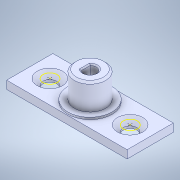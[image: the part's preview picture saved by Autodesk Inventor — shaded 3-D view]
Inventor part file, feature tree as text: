
AUTODESK INVENTOR PART (.ipt)
format: ipt  version: 2021 (Build 250183000, 183)  size: 167,424 bytes
history: native  units: in
note: dims shown in document units (in); Inventor stores cm internally (conversion verified against a paired STEP export)
features: sketch x5, extrude x3, other x3, chamfer x2, reference x2, hole x1, projected_geometry x1
ambient origin geometry x8: Origin, YZ Plane, XZ Plane, XY Plane, X Axis, Y Axis, Z Axis, Center Point
bodies: Solid1 (feature_tree)
feature tree (17):
  extrude  "Extrusion1"  Depth=0.3937in TaperAngle=0.0deg
  extrude  "Extrusion2"  Depth=0.3937in TaperAngle=0.0deg
  extrude  "Extrusion3"  Depth=0.002in
  chamfer  "Chamfer1"  Distance=0.0118in Angle=45.0deg
  sketch  "Sketch4"  dims[d19=0.1339in d20=0.2362in d21=0.248in d22=0.0787in d23=90.0deg d24=0.315in d25=0.0in d26=0.002in]
  hole  "Hole2"  [1 undecoded]
  chamfer  "Chamfer2"  [1 undecoded]
  sketch  "Sketch1"  dims[d1=0.3937in d2=0.0in d3=0.3937in d4=0.0in]
  projected_geometry  "Projected Loop1"
  sketch  "Sketch2"  dims[d5=0.0039in d6=0.3937in d7=0.0in]
  sketch  "Sketch3"  dims[d8=0.0197in d9=0.0787in d10=45.0deg]
  reference  "Reference1"
  reference  "Reference2"
  sketch  "Sketch6"  dims[d27=0.002in d28=0.0118in d29=0.0787in d30=45.0deg]
  other  "CSK for M4 Countersunk Flat Head Screw1"
  other  "sub_assy_robot_arm_link1.iam"
  other  "arm_1_v2:1"
note: 2 required parameter values undecoded (feature->parameter linkage not recoverable at this tier; creation-order binding heuristic only, values carry confidence <= 0.55)
